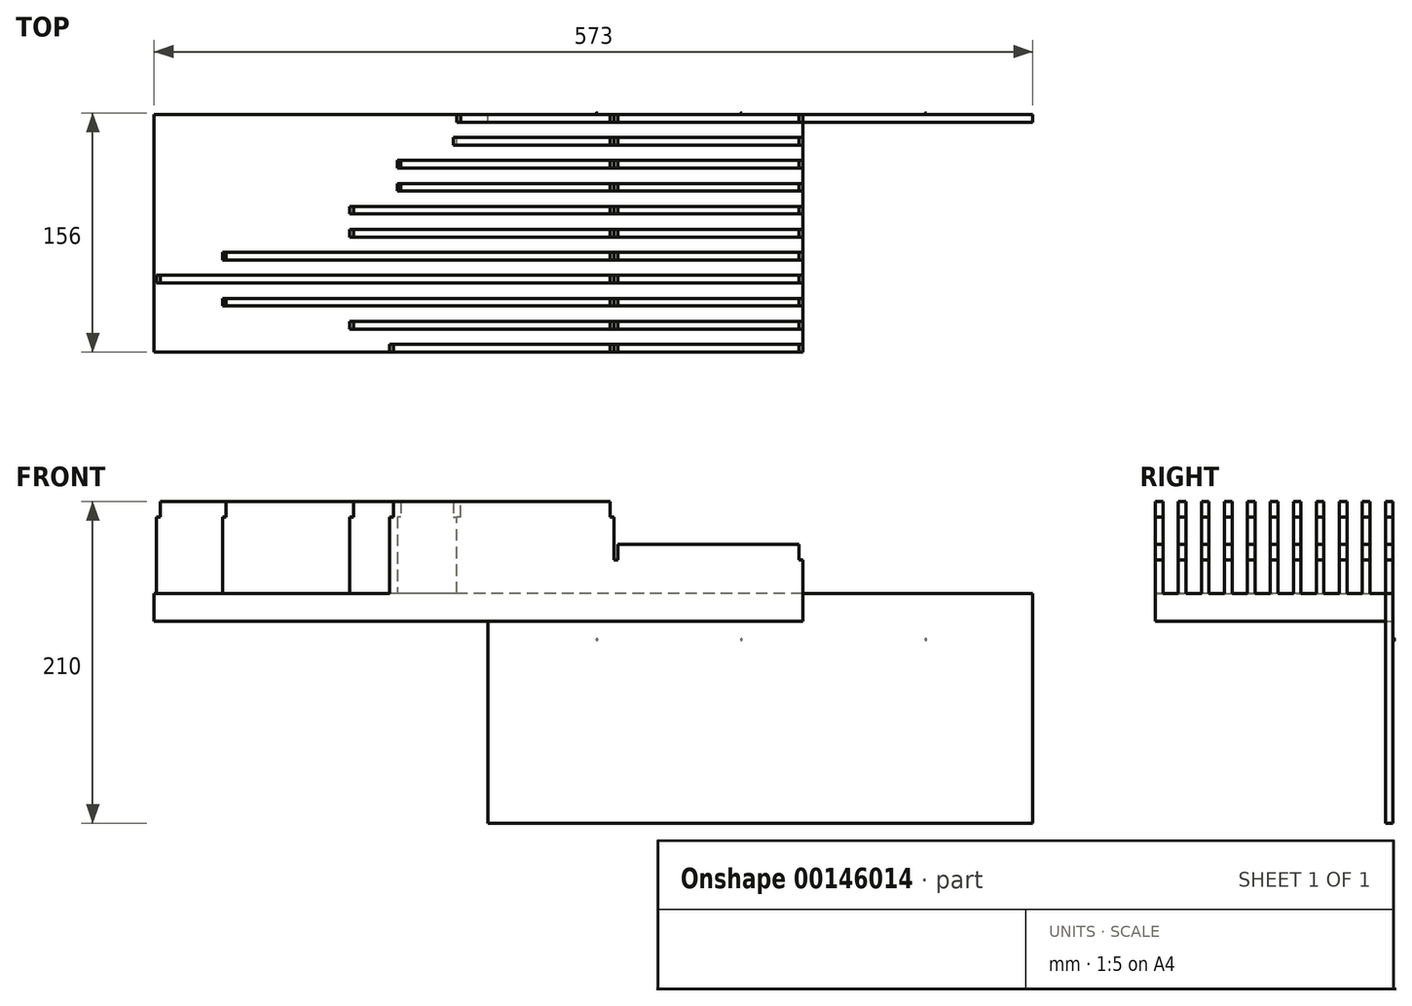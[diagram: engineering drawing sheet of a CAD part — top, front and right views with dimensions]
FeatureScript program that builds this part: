
annotation { "Feature Type Name" : "Feature", "Feature Type Description" : "" }
export const myFeature = defineFeature(function(context is Context, id is Id, definition is map)
    precondition{}
    {
        {
            var Q0;
            Q0=qCreatedBy(makeId("Right.planeOp"),FACE);
            var sketch = newSketch(context, id + "F0", { "sketchPlane" : qUnion([Q0])});
            skLineSegment(sketch, "E0", {"start": v(174.28, 60) * mm, "end": v(179.28, 60) * mm});
            skLineSegment(sketch, "E1", {"start": v(179.28, 60) * mm, "end": v(179.28, 0) * mm});
            skLineSegment(sketch, "E2", {"start": v(179.28, 0) * mm, "end": v(189.28, 0) * mm});
            skLineSegment(sketch, "E3", {"start": v(189.28, 0) * mm, "end": v(189.28, 60) * mm});
            skLineSegment(sketch, "E4", {"start": v(189.28, 60) * mm, "end": v(194.28, 60) * mm});
            skLineSegment(sketch, "E5", {"start": v(194.28, 60) * mm, "end": v(194.28, 0) * mm});
            skLineSegment(sketch, "E6", {"start": v(194.28, 0) * mm, "end": v(204.28, 0) * mm});
            skLineSegment(sketch, "E7", {"start": v(204.28, 0) * mm, "end": v(204.28, 60) * mm});
            skLineSegment(sketch, "E8", {"start": v(204.28, 60) * mm, "end": v(209.28, 60) * mm});
            skLineSegment(sketch, "E9", {"start": v(209.28, 60) * mm, "end": v(209.28, 0) * mm});
            skLineSegment(sketch, "E10", {"start": v(209.28, 0) * mm, "end": v(219.28, 0) * mm});
            skLineSegment(sketch, "E11", {"start": v(219.28, 0) * mm, "end": v(219.28, 60) * mm});
            skLineSegment(sketch, "E12", {"start": v(219.28, 60) * mm, "end": v(224.28, 60) * mm});
            skLineSegment(sketch, "E13", {"start": v(224.28, 60) * mm, "end": v(224.28, 0) * mm});
            skLineSegment(sketch, "E14", {"start": v(224.28, 0) * mm, "end": v(234.28, 0) * mm});
            skLineSegment(sketch, "E15", {"start": v(234.28, 0) * mm, "end": v(234.28, 60) * mm});
            skLineSegment(sketch, "E16", {"start": v(234.28, 60) * mm, "end": v(239.28, 60) * mm});
            skLineSegment(sketch, "E17", {"start": v(239.28, 60) * mm, "end": v(239.28, 0) * mm});
            skLineSegment(sketch, "E18", {"start": v(239.28, 0) * mm, "end": v(249.28, 0) * mm});
            skLineSegment(sketch, "E19", {"start": v(249.28, 0) * mm, "end": v(249.28, 60) * mm});
            skLineSegment(sketch, "E20", {"start": v(249.28, 60) * mm, "end": v(254.28, 60) * mm});
            skLineSegment(sketch, "E21", {"start": v(254.28, 60) * mm, "end": v(254.28, 0) * mm});
            skLineSegment(sketch, "E22", {"start": v(254.28, 0) * mm, "end": v(264.28, 0) * mm});
            skLineSegment(sketch, "E23", {"start": v(264.28, 0) * mm, "end": v(264.28, 60) * mm});
            skLineSegment(sketch, "E24", {"start": v(264.28, 60) * mm, "end": v(269.28, 60) * mm});
            skLineSegment(sketch, "E25", {"start": v(269.28, 60) * mm, "end": v(269.28, 0) * mm});
            skLineSegment(sketch, "E26", {"start": v(269.28, 0) * mm, "end": v(279.28, 0) * mm});
            skLineSegment(sketch, "E27", {"start": v(279.28, 0) * mm, "end": v(279.28, 60) * mm});
            skLineSegment(sketch, "E28", {"start": v(279.28, 60) * mm, "end": v(284.28, 60) * mm});
            skLineSegment(sketch, "E29", {"start": v(284.28, 60) * mm, "end": v(284.28, 0) * mm});
            skLineSegment(sketch, "E30", {"start": v(284.28, 0) * mm, "end": v(294.28, 0) * mm});
            skLineSegment(sketch, "E31", {"start": v(294.28, 0) * mm, "end": v(294.28, 60) * mm});
            skLineSegment(sketch, "E32", {"start": v(294.28, 60) * mm, "end": v(299.28, 60) * mm});
            skLineSegment(sketch, "E33", {"start": v(299.28, 60) * mm, "end": v(299.28, 0) * mm});
            skLineSegment(sketch, "E34", {"start": v(299.28, 0) * mm, "end": v(309.28, 0) * mm});
            skLineSegment(sketch, "E35", {"start": v(309.28, 0) * mm, "end": v(309.28, 60) * mm});
            skLineSegment(sketch, "E36", {"start": v(309.28, 60) * mm, "end": v(314.28, 60) * mm});
            skLineSegment(sketch, "E37", {"start": v(314.28, 60) * mm, "end": v(314.28, 0) * mm});
            skLineSegment(sketch, "E38", {"start": v(314.28, 0) * mm, "end": v(324.28, 0) * mm});
            skLineSegment(sketch, "E39", {"start": v(324.28, 0) * mm, "end": v(324.28, 60) * mm});
            skLineSegment(sketch, "E40", {"start": v(324.28, 60) * mm, "end": v(329.28, 60) * mm});
            skLineSegment(sketch, "E41", {"start": v(329.28, 60) * mm, "end": v(329.28, 60) * mm});
            skLineSegment(sketch, "E42", {"start": v(324.28, -18.06) * mm, "end": v(174.24, -18.06) * mm});
            skLineSegment(sketch, "E43", {"start": v(329.28, 60) * mm, "end": v(329.28, -150) * mm});
            skLineSegment(sketch, "E44", {"start": v(329.28, -150) * mm, "end": v(324.28, -150) * mm});
            skLineSegment(sketch, "E45", {"start": v(324.28, -150) * mm, "end": v(324.28, -18.06) * mm});
            skLineSegment(sketch, "E46", {"start": v(174.28, 60) * mm, "end": v(174.28, -18.06) * mm});
            skSolve(sketch);
        }
        {
            var Q0;
            Q0=makeQuery(id+"F0.imprint","IMPRINT",FACE,{"disambiguationData":[TD([[makeQuery(id+"F0.imprint","IMPRINT",EDGE,{"derivedFrom":sQuery(id+"F0.wireOp",EDGE,"RiP20wC8-9t7q-gec1-XB14-b4tMjAQ6knOq")}),-1.0]])]});
            var Q1;
            Q1=makeQuery(id+"F0.imprint","IMPRINT",FACE,{"disambiguationData":[TD([[makeQuery(id+"F0.imprint","IMPRINT",EDGE,{"derivedFrom":sQuery(id+"F0.wireOp",EDGE,"E0")}),-1.0]])]});
            extrude(context, id + "F1", {"entities" : qUnion([Q0, Q1]), "depth" : 123 * mm});
        }
        {
            var Q0;
            Q0 = qSketchRegion(id + "F0", true);
            extrude(context, id + "F2", {"entities" : qUnion([Q0]), "operationType" : NewBodyOperationType.ADD, "oppositeDirection" : true, "depth" : 300 * mm});
        }
        {
            var Q0;
            Q0=makeQuery(id+"F1.opExtrude","SWEPT_FACE",FACE,{"disambiguationData":[OSD([sQuery(id+"F0.wireOp",EDGE,"E43")])]});
            var sketch = newSketch(context, id + "F3", { "sketchPlane" : qUnion([Q0])});
            skCircle(sketch, "E47", {"center": v(-203.34, -30) * mm, "radius": 0.5 * mm});
            skCircle(sketch, "E48", {"center": v(-83.06, -30) * mm, "radius": 0.5 * mm});
            skCircle(sketch, "E49", {"center": v(11.19, -30) * mm, "radius": 0.5 * mm});
            skSolve(sketch);
        }
        {
            var Q0;
            Q0 = qSketchRegion(id + "F3", true);
            extrude(context, id + "F4", {"entities" : qUnion([Q0]), "operationType" : NewBodyOperationType.ADD, "depth" : 1 * mm});
        }
        {
            var Q0;
            Q0=makeQuery(id+"F1.opExtrude","SWEPT_FACE",FACE,{"disambiguationData":[OSD([sQuery(id+"F0.wireOp",EDGE,"E43")])]});
            var sketch = newSketch(context, id + "F5", { "sketchPlane" : qUnion([Q0])});
            skLineSegment(sketch, "E50.bottom", {"start": v(-123, 60) * mm, "end": v(0, 60) * mm});
            skLineSegment(sketch, "E50.top", {"start": v(-123, 32) * mm, "end": v(0, 32) * mm});
            skLineSegment(sketch, "E50.left", {"start": v(-123, 60) * mm, "end": v(-123, 32) * mm});
            skLineSegment(sketch, "E50.right", {"start": v(0, 60) * mm, "end": v(0, 32) * mm});
            skSolve(sketch);
        }
        {
            var Q0;
            Q0 = qSketchRegion(id + "F5", true);
            extrude(context, id + "F6", {"entities" : qUnion([Q0]), "operationType" : NewBodyOperationType.REMOVE, "oppositeDirection" : true, "depth" : 300 * mm});
        }
        {
            var Q0;
            Q0=makeQuery(id+"F1.opExtrude","SWEPT_FACE",FACE,{"disambiguationData":[OSD([sQuery(id+"F0.wireOp",EDGE,"E43")])]});
            var sketch = newSketch(context, id + "F7", { "sketchPlane" : qUnion([Q0])});
            skLineSegment(sketch, "E51.bottom", {"start": v(0, 32) * mm, "end": v(-2.5, 32) * mm});
            skLineSegment(sketch, "E51.top", {"start": v(0, 22) * mm, "end": v(-2.5, 22) * mm});
            skLineSegment(sketch, "E51.left", {"start": v(0, 32) * mm, "end": v(0, 22) * mm});
            skLineSegment(sketch, "E51.right", {"start": v(-2.5, 32) * mm, "end": v(-2.5, 22) * mm});
            skLineSegment(sketch, "E52.bottom", {"start": v(0, 60) * mm, "end": v(2.5, 60) * mm});
            skLineSegment(sketch, "E52.top", {"start": v(0, 50) * mm, "end": v(2.5, 50) * mm});
            skLineSegment(sketch, "E52.left", {"start": v(0, 60) * mm, "end": v(0, 50) * mm});
            skLineSegment(sketch, "E52.right", {"start": v(2.5, 60) * mm, "end": v(2.5, 50) * mm});
            skLineSegment(sketch, "E53.bottom", {"start": v(-123, 32) * mm, "end": v(-120.5, 32) * mm});
            skLineSegment(sketch, "E53.top", {"start": v(-123, 22) * mm, "end": v(-120.5, 22) * mm});
            skLineSegment(sketch, "E53.left", {"start": v(-123, 32) * mm, "end": v(-123, 22) * mm});
            skLineSegment(sketch, "E53.right", {"start": v(-120.5, 32) * mm, "end": v(-120.5, 22) * mm});
            skSolve(sketch);
        }
        {
            var Q0;
            Q0=makeQuery(id+"F7.imprint","IMPRINT",FACE,{"disambiguationData":[TD([[makeQuery(id+"F7.imprint","IMPRINT",EDGE,{"derivedFrom":sQuery(id+"F7.wireOp",EDGE,"E51.bottom")}),-1.0]])]});
            var Q1;
            Q1=makeQuery(id+"F7.imprint","IMPRINT",FACE,{"disambiguationData":[TD([[makeQuery(id+"F7.imprint","IMPRINT",EDGE,{"derivedFrom":sQuery(id+"F7.wireOp",EDGE,"E52.bottom")}),-1.0]])]});
            var Q2;
            Q2=makeQuery(id+"F7.imprint","IMPRINT",FACE,{"disambiguationData":[TD([[makeQuery(id+"F7.imprint","IMPRINT",EDGE,{"derivedFrom":sQuery(id+"F7.wireOp",EDGE,"E53.bottom")}),-1.0]])]});
            extrude(context, id + "F8", {"entities" : qUnion([Q0, Q1, Q2]), "operationType" : NewBodyOperationType.REMOVE, "oppositeDirection" : true, "depth" : 300 * mm});
        }
        {
            var Q0;
            Q0=makeQuery(id+"F1.opExtrude","SWEPT_FACE",FACE,{"disambiguationData":[OSD([sQuery(id+"F0.wireOp",EDGE,"E43")])]});
            var sketch = newSketch(context, id + "F9", { "sketchPlane" : qUnion([Q0])});
            skLineSegment(sketch, "E54.bottom", {"start": v(-123, -150) * mm, "end": v(-273, -150) * mm});
            skLineSegment(sketch, "E54.top", {"start": v(-123, 0) * mm, "end": v(-273, 0) * mm});
            skLineSegment(sketch, "E54.left", {"start": v(-123, -150) * mm, "end": v(-123, 0) * mm});
            skLineSegment(sketch, "E54.right", {"start": v(-273, -150) * mm, "end": v(-273, 0) * mm});
            skSolve(sketch);
        }
        {
            var Q0;
            Q0 = qSketchRegion(id + "F9", true);
            extrude(context, id + "F10", {"entities" : qUnion([Q0]), "operationType" : NewBodyOperationType.ADD, "oppositeDirection" : true, "depth" : 5 * mm});
        }
        {
            var Q0;
            Q0=makeQuery(id+"F2.opExtrude","CAP_FACE",FACE,{"disambiguationData":[OSD([sQuery(id+"F0.wireOp",EDGE,"E0"),sQuery(id+"F0.wireOp",EDGE,"E1"),sQuery(id+"F0.wireOp",EDGE,"E2"),sQuery(id+"F0.wireOp",EDGE,"E3"),sQuery(id+"F0.wireOp",EDGE,"E4"),sQuery(id+"F0.wireOp",EDGE,"E5"),sQuery(id+"F0.wireOp",EDGE,"E6"),sQuery(id+"F0.wireOp",EDGE,"E7"),sQuery(id+"F0.wireOp",EDGE,"E8"),sQuery(id+"F0.wireOp",EDGE,"E9"),sQuery(id+"F0.wireOp",EDGE,"E10"),sQuery(id+"F0.wireOp",EDGE,"E11"),sQuery(id+"F0.wireOp",EDGE,"E12"),sQuery(id+"F0.wireOp",EDGE,"E13"),sQuery(id+"F0.wireOp",EDGE,"E14"),sQuery(id+"F0.wireOp",EDGE,"E15"),sQuery(id+"F0.wireOp",EDGE,"E16"),sQuery(id+"F0.wireOp",EDGE,"E17"),sQuery(id+"F0.wireOp",EDGE,"E18"),sQuery(id+"F0.wireOp",EDGE,"E19"),sQuery(id+"F0.wireOp",EDGE,"E20"),sQuery(id+"F0.wireOp",EDGE,"E21"),sQuery(id+"F0.wireOp",EDGE,"E22"),sQuery(id+"F0.wireOp",EDGE,"E23"),sQuery(id+"F0.wireOp",EDGE,"E24"),sQuery(id+"F0.wireOp",EDGE,"E25"),sQuery(id+"F0.wireOp",EDGE,"E26"),sQuery(id+"F0.wireOp",EDGE,"E27"),sQuery(id+"F0.wireOp",EDGE,"E28"),sQuery(id+"F0.wireOp",EDGE,"E29"),sQuery(id+"F0.wireOp",EDGE,"E30"),sQuery(id+"F0.wireOp",EDGE,"E31"),sQuery(id+"F0.wireOp",EDGE,"E32"),sQuery(id+"F0.wireOp",EDGE,"E33"),sQuery(id+"F0.wireOp",EDGE,"E34"),sQuery(id+"F0.wireOp",EDGE,"E35"),sQuery(id+"F0.wireOp",EDGE,"E36"),sQuery(id+"F0.wireOp",EDGE,"E37"),sQuery(id+"F0.wireOp",EDGE,"E38"),sQuery(id+"F0.wireOp",EDGE,"E39"),sQuery(id+"F0.wireOp",EDGE,"E40"),sQuery(id+"F0.wireOp",EDGE,"E42"),sQuery(id+"F0.wireOp",EDGE,"E43"),sQuery(id+"F0.wireOp",EDGE,"E44"),sQuery(id+"F0.wireOp",EDGE,"E45"),sQuery(id+"F0.wireOp",EDGE,"E46")])],"isStart":false});
            var sketch = newSketch(context, id + "F11", { "sketchPlane" : qUnion([Q0])});
            skLineSegment(sketch, "E55.bottom", {"start": v(-309.28, 0) * mm, "end": v(-329.28, 0) * mm});
            skLineSegment(sketch, "E55.top", {"start": v(-309.28, 60) * mm, "end": v(-329.28, 60) * mm});
            skLineSegment(sketch, "E55.left", {"start": v(-309.28, 0) * mm, "end": v(-309.28, 60) * mm});
            skLineSegment(sketch, "E55.right", {"start": v(-329.28, 0) * mm, "end": v(-329.28, 60) * mm});
            skSolve(sketch);
        }
        {
            var Q0;
            {var subQ2=sQuery(id+"F11.wireOp",EDGE,"E55.right");Q0=makeQuery(id+"F11.imprint","IMPRINT",FACE,{"disambiguationData":[TD([[makeQuery(id+"F11.imprint","IMPRINT",EDGE,{"derivedFrom":subQ2}),1.0]])]});}
            var Q1;
            {var subQ0=sQuery(id+"F11.wireOp",EDGE,"E55.left");Q1=makeQuery(id+"F11.imprint","IMPRINT",FACE,{"disambiguationData":[TD([[makeQuery(id+"F11.imprint","IMPRINT",EDGE,{"derivedFrom":subQ0}),1.0]])]});}
            extrude(context, id + "F12", {"entities" : qUnion([Q0, Q1]), "operationType" : NewBodyOperationType.REMOVE, "oppositeDirection" : true, "depth" : 197.5 * mm});
        }
        {
            var Q0;
            Q0=makeQuery(id+"F2.opExtrude","CAP_FACE",FACE,{"disambiguationData":[OSD([sQuery(id+"F0.wireOp",EDGE,"E0"),sQuery(id+"F0.wireOp",EDGE,"E1"),sQuery(id+"F0.wireOp",EDGE,"E2"),sQuery(id+"F0.wireOp",EDGE,"E3"),sQuery(id+"F0.wireOp",EDGE,"E4"),sQuery(id+"F0.wireOp",EDGE,"E5"),sQuery(id+"F0.wireOp",EDGE,"E6"),sQuery(id+"F0.wireOp",EDGE,"E7"),sQuery(id+"F0.wireOp",EDGE,"E8"),sQuery(id+"F0.wireOp",EDGE,"E9"),sQuery(id+"F0.wireOp",EDGE,"E10"),sQuery(id+"F0.wireOp",EDGE,"E11"),sQuery(id+"F0.wireOp",EDGE,"E12"),sQuery(id+"F0.wireOp",EDGE,"E13"),sQuery(id+"F0.wireOp",EDGE,"E14"),sQuery(id+"F0.wireOp",EDGE,"E15"),sQuery(id+"F0.wireOp",EDGE,"E16"),sQuery(id+"F0.wireOp",EDGE,"E17"),sQuery(id+"F0.wireOp",EDGE,"E18"),sQuery(id+"F0.wireOp",EDGE,"E19"),sQuery(id+"F0.wireOp",EDGE,"E20"),sQuery(id+"F0.wireOp",EDGE,"E21"),sQuery(id+"F0.wireOp",EDGE,"E22"),sQuery(id+"F0.wireOp",EDGE,"E23"),sQuery(id+"F0.wireOp",EDGE,"E24"),sQuery(id+"F0.wireOp",EDGE,"E25"),sQuery(id+"F0.wireOp",EDGE,"E26"),sQuery(id+"F0.wireOp",EDGE,"E27"),sQuery(id+"F0.wireOp",EDGE,"E28"),sQuery(id+"F0.wireOp",EDGE,"E29"),sQuery(id+"F0.wireOp",EDGE,"E30"),sQuery(id+"F0.wireOp",EDGE,"E31"),sQuery(id+"F0.wireOp",EDGE,"E32"),sQuery(id+"F0.wireOp",EDGE,"E33"),sQuery(id+"F0.wireOp",EDGE,"E34"),sQuery(id+"F0.wireOp",EDGE,"E35"),sQuery(id+"F0.wireOp",EDGE,"E36"),sQuery(id+"F0.wireOp",EDGE,"E37"),sQuery(id+"F0.wireOp",EDGE,"E38"),sQuery(id+"F0.wireOp",EDGE,"E39"),sQuery(id+"F0.wireOp",EDGE,"E40"),sQuery(id+"F0.wireOp",EDGE,"E42"),sQuery(id+"F0.wireOp",EDGE,"E43"),sQuery(id+"F0.wireOp",EDGE,"E44"),sQuery(id+"F0.wireOp",EDGE,"E45"),sQuery(id+"F0.wireOp",EDGE,"E46")])],"isStart":false});
            var sketch = newSketch(context, id + "F13", { "sketchPlane" : qUnion([Q0])});
            skLineSegment(sketch, "E56.bottom", {"start": v(-279.28, 0) * mm, "end": v(-299.28, 0) * mm});
            skLineSegment(sketch, "E56.top", {"start": v(-279.28, 60) * mm, "end": v(-299.28, 60) * mm});
            skLineSegment(sketch, "E56.left", {"start": v(-279.28, 0) * mm, "end": v(-279.28, 60) * mm});
            skLineSegment(sketch, "E56.right", {"start": v(-299.28, 0) * mm, "end": v(-299.28, 60) * mm});
            skSolve(sketch);
        }
        {
            var Q0;
            Q0 = qSketchRegion(id + "F13", true);
            extrude(context, id + "F14", {"entities" : qUnion([Q0]), "operationType" : NewBodyOperationType.REMOVE, "oppositeDirection" : true, "depth" : 158.5 * mm});
        }
        {
            var Q0;
            Q0=makeQuery(id+"F2.opExtrude","CAP_FACE",FACE,{"disambiguationData":[OSD([sQuery(id+"F0.wireOp",EDGE,"E0"),sQuery(id+"F0.wireOp",EDGE,"E1"),sQuery(id+"F0.wireOp",EDGE,"E2"),sQuery(id+"F0.wireOp",EDGE,"E3"),sQuery(id+"F0.wireOp",EDGE,"E4"),sQuery(id+"F0.wireOp",EDGE,"E5"),sQuery(id+"F0.wireOp",EDGE,"E6"),sQuery(id+"F0.wireOp",EDGE,"E7"),sQuery(id+"F0.wireOp",EDGE,"E8"),sQuery(id+"F0.wireOp",EDGE,"E9"),sQuery(id+"F0.wireOp",EDGE,"E10"),sQuery(id+"F0.wireOp",EDGE,"E11"),sQuery(id+"F0.wireOp",EDGE,"E12"),sQuery(id+"F0.wireOp",EDGE,"E13"),sQuery(id+"F0.wireOp",EDGE,"E14"),sQuery(id+"F0.wireOp",EDGE,"E15"),sQuery(id+"F0.wireOp",EDGE,"E16"),sQuery(id+"F0.wireOp",EDGE,"E17"),sQuery(id+"F0.wireOp",EDGE,"E18"),sQuery(id+"F0.wireOp",EDGE,"E19"),sQuery(id+"F0.wireOp",EDGE,"E20"),sQuery(id+"F0.wireOp",EDGE,"E21"),sQuery(id+"F0.wireOp",EDGE,"E22"),sQuery(id+"F0.wireOp",EDGE,"E23"),sQuery(id+"F0.wireOp",EDGE,"E24"),sQuery(id+"F0.wireOp",EDGE,"E25"),sQuery(id+"F0.wireOp",EDGE,"E26"),sQuery(id+"F0.wireOp",EDGE,"E27"),sQuery(id+"F0.wireOp",EDGE,"E28"),sQuery(id+"F0.wireOp",EDGE,"E29"),sQuery(id+"F0.wireOp",EDGE,"E30"),sQuery(id+"F0.wireOp",EDGE,"E31"),sQuery(id+"F0.wireOp",EDGE,"E32"),sQuery(id+"F0.wireOp",EDGE,"E33"),sQuery(id+"F0.wireOp",EDGE,"E34"),sQuery(id+"F0.wireOp",EDGE,"E35"),sQuery(id+"F0.wireOp",EDGE,"E36"),sQuery(id+"F0.wireOp",EDGE,"E37"),sQuery(id+"F0.wireOp",EDGE,"E38"),sQuery(id+"F0.wireOp",EDGE,"E39"),sQuery(id+"F0.wireOp",EDGE,"E40"),sQuery(id+"F0.wireOp",EDGE,"E42"),sQuery(id+"F0.wireOp",EDGE,"E43"),sQuery(id+"F0.wireOp",EDGE,"E44"),sQuery(id+"F0.wireOp",EDGE,"E45"),sQuery(id+"F0.wireOp",EDGE,"E46")])],"isStart":false});
            var sketch = newSketch(context, id + "F15", { "sketchPlane" : qUnion([Q0])});
            skLineSegment(sketch, "E57.bottom", {"start": v(-269.28, 60) * mm, "end": v(-249.28, 60) * mm});
            skLineSegment(sketch, "E57.top", {"start": v(-269.28, 0) * mm, "end": v(-249.28, 0) * mm});
            skLineSegment(sketch, "E57.left", {"start": v(-269.28, 60) * mm, "end": v(-269.28, 0) * mm});
            skLineSegment(sketch, "E57.right", {"start": v(-249.28, 60) * mm, "end": v(-249.28, 0) * mm});
            skLineSegment(sketch, "E58.bottom", {"start": v(-194.28, 0) * mm, "end": v(-189.28, 0) * mm});
            skLineSegment(sketch, "E58.top", {"start": v(-194.28, 60) * mm, "end": v(-189.28, 60) * mm});
            skLineSegment(sketch, "E58.left", {"start": v(-194.28, 0) * mm, "end": v(-194.28, 60) * mm});
            skLineSegment(sketch, "E58.right", {"start": v(-189.28, 0) * mm, "end": v(-189.28, 60) * mm});
            skSolve(sketch);
        }
        {
            var Q0;
            Q0 = qSketchRegion(id + "F15", true);
            extrude(context, id + "F16", {"entities" : qUnion([Q0]), "operationType" : NewBodyOperationType.REMOVE, "oppositeDirection" : true, "depth" : 127.5 * mm});
        }
        {
            var Q0;
            Q0=makeQuery(id+"F2.opExtrude","CAP_FACE",FACE,{"disambiguationData":[OSD([sQuery(id+"F0.wireOp",EDGE,"E0"),sQuery(id+"F0.wireOp",EDGE,"E1"),sQuery(id+"F0.wireOp",EDGE,"E2"),sQuery(id+"F0.wireOp",EDGE,"E3"),sQuery(id+"F0.wireOp",EDGE,"E4"),sQuery(id+"F0.wireOp",EDGE,"E5"),sQuery(id+"F0.wireOp",EDGE,"E6"),sQuery(id+"F0.wireOp",EDGE,"E7"),sQuery(id+"F0.wireOp",EDGE,"E8"),sQuery(id+"F0.wireOp",EDGE,"E9"),sQuery(id+"F0.wireOp",EDGE,"E10"),sQuery(id+"F0.wireOp",EDGE,"E11"),sQuery(id+"F0.wireOp",EDGE,"E12"),sQuery(id+"F0.wireOp",EDGE,"E13"),sQuery(id+"F0.wireOp",EDGE,"E14"),sQuery(id+"F0.wireOp",EDGE,"E15"),sQuery(id+"F0.wireOp",EDGE,"E16"),sQuery(id+"F0.wireOp",EDGE,"E17"),sQuery(id+"F0.wireOp",EDGE,"E18"),sQuery(id+"F0.wireOp",EDGE,"E19"),sQuery(id+"F0.wireOp",EDGE,"E20"),sQuery(id+"F0.wireOp",EDGE,"E21"),sQuery(id+"F0.wireOp",EDGE,"E22"),sQuery(id+"F0.wireOp",EDGE,"E23"),sQuery(id+"F0.wireOp",EDGE,"E24"),sQuery(id+"F0.wireOp",EDGE,"E25"),sQuery(id+"F0.wireOp",EDGE,"E26"),sQuery(id+"F0.wireOp",EDGE,"E27"),sQuery(id+"F0.wireOp",EDGE,"E28"),sQuery(id+"F0.wireOp",EDGE,"E29"),sQuery(id+"F0.wireOp",EDGE,"E30"),sQuery(id+"F0.wireOp",EDGE,"E31"),sQuery(id+"F0.wireOp",EDGE,"E32"),sQuery(id+"F0.wireOp",EDGE,"E33"),sQuery(id+"F0.wireOp",EDGE,"E34"),sQuery(id+"F0.wireOp",EDGE,"E35"),sQuery(id+"F0.wireOp",EDGE,"E36"),sQuery(id+"F0.wireOp",EDGE,"E37"),sQuery(id+"F0.wireOp",EDGE,"E38"),sQuery(id+"F0.wireOp",EDGE,"E39"),sQuery(id+"F0.wireOp",EDGE,"E40"),sQuery(id+"F0.wireOp",EDGE,"E42"),sQuery(id+"F0.wireOp",EDGE,"E43"),sQuery(id+"F0.wireOp",EDGE,"E44"),sQuery(id+"F0.wireOp",EDGE,"E45"),sQuery(id+"F0.wireOp",EDGE,"E46")])],"isStart":false});
            var sketch = newSketch(context, id + "F17", { "sketchPlane" : qUnion([Q0])});
            skLineSegment(sketch, "E59.bottom", {"start": v(-239.28, 60) * mm, "end": v(-234.28, 60) * mm});
            skLineSegment(sketch, "E59.top", {"start": v(-239.28, 0) * mm, "end": v(-234.28, 0) * mm});
            skLineSegment(sketch, "E59.left", {"start": v(-239.28, 60) * mm, "end": v(-239.28, 0) * mm});
            skLineSegment(sketch, "E59.right", {"start": v(-234.28, 60) * mm, "end": v(-234.28, 0) * mm});
            skLineSegment(sketch, "E60.bottom", {"start": v(-209.28, 60) * mm, "end": v(-204.28, 60) * mm});
            skLineSegment(sketch, "E60.top", {"start": v(-209.28, 0) * mm, "end": v(-204.28, 0) * mm});
            skLineSegment(sketch, "E60.left", {"start": v(-209.28, 60) * mm, "end": v(-209.28, 0) * mm});
            skLineSegment(sketch, "E60.right", {"start": v(-204.28, 60) * mm, "end": v(-204.28, 0) * mm});
            skSolve(sketch);
        }
        {
            var Q0;
            Q0 = qSketchRegion(id + "F17", true);
            extrude(context, id + "F18", {"entities" : qUnion([Q0]), "operationType" : NewBodyOperationType.REMOVE, "oppositeDirection" : true, "depth" : 44.5 * mm});
        }
        {
            var Q0;
            Q0=makeQuery(id+"F2.opExtrude","CAP_FACE",FACE,{"disambiguationData":[OSD([sQuery(id+"F0.wireOp",EDGE,"E0"),sQuery(id+"F0.wireOp",EDGE,"E1"),sQuery(id+"F0.wireOp",EDGE,"E2"),sQuery(id+"F0.wireOp",EDGE,"E3"),sQuery(id+"F0.wireOp",EDGE,"E4"),sQuery(id+"F0.wireOp",EDGE,"E5"),sQuery(id+"F0.wireOp",EDGE,"E6"),sQuery(id+"F0.wireOp",EDGE,"E7"),sQuery(id+"F0.wireOp",EDGE,"E8"),sQuery(id+"F0.wireOp",EDGE,"E9"),sQuery(id+"F0.wireOp",EDGE,"E10"),sQuery(id+"F0.wireOp",EDGE,"E11"),sQuery(id+"F0.wireOp",EDGE,"E12"),sQuery(id+"F0.wireOp",EDGE,"E13"),sQuery(id+"F0.wireOp",EDGE,"E14"),sQuery(id+"F0.wireOp",EDGE,"E15"),sQuery(id+"F0.wireOp",EDGE,"E16"),sQuery(id+"F0.wireOp",EDGE,"E17"),sQuery(id+"F0.wireOp",EDGE,"E18"),sQuery(id+"F0.wireOp",EDGE,"E19"),sQuery(id+"F0.wireOp",EDGE,"E20"),sQuery(id+"F0.wireOp",EDGE,"E21"),sQuery(id+"F0.wireOp",EDGE,"E22"),sQuery(id+"F0.wireOp",EDGE,"E23"),sQuery(id+"F0.wireOp",EDGE,"E24"),sQuery(id+"F0.wireOp",EDGE,"E25"),sQuery(id+"F0.wireOp",EDGE,"E26"),sQuery(id+"F0.wireOp",EDGE,"E27"),sQuery(id+"F0.wireOp",EDGE,"E28"),sQuery(id+"F0.wireOp",EDGE,"E29"),sQuery(id+"F0.wireOp",EDGE,"E30"),sQuery(id+"F0.wireOp",EDGE,"E31"),sQuery(id+"F0.wireOp",EDGE,"E32"),sQuery(id+"F0.wireOp",EDGE,"E33"),sQuery(id+"F0.wireOp",EDGE,"E34"),sQuery(id+"F0.wireOp",EDGE,"E35"),sQuery(id+"F0.wireOp",EDGE,"E36"),sQuery(id+"F0.wireOp",EDGE,"E37"),sQuery(id+"F0.wireOp",EDGE,"E38"),sQuery(id+"F0.wireOp",EDGE,"E39"),sQuery(id+"F0.wireOp",EDGE,"E40"),sQuery(id+"F0.wireOp",EDGE,"E42"),sQuery(id+"F0.wireOp",EDGE,"E43"),sQuery(id+"F0.wireOp",EDGE,"E44"),sQuery(id+"F0.wireOp",EDGE,"E45"),sQuery(id+"F0.wireOp",EDGE,"E46")])],"isStart":false});
            var sketch = newSketch(context, id + "F19", { "sketchPlane" : qUnion([Q0])});
            skLineSegment(sketch, "E61.bottom", {"start": v(-219.28, 0) * mm, "end": v(-224.28, 0) * mm});
            skLineSegment(sketch, "E61.top", {"start": v(-219.28, 60) * mm, "end": v(-224.28, 60) * mm});
            skLineSegment(sketch, "E61.left", {"start": v(-219.28, 0) * mm, "end": v(-219.28, 60) * mm});
            skLineSegment(sketch, "E61.right", {"start": v(-224.28, 0) * mm, "end": v(-224.28, 60) * mm});
            skSolve(sketch);
        }
        {
            var Q0;
            Q0 = qSketchRegion(id + "F19", true);
            extrude(context, id + "F20", {"entities" : qUnion([Q0]), "operationType" : NewBodyOperationType.REMOVE, "oppositeDirection" : true, "depth" : 1.5 * mm});
        }
        {
            var Q0;
            Q0=makeQuery(id+"F2.opExtrude","CAP_FACE",FACE,{"disambiguationData":[OSD([sQuery(id+"F0.wireOp",EDGE,"E0"),sQuery(id+"F0.wireOp",EDGE,"E1"),sQuery(id+"F0.wireOp",EDGE,"E2"),sQuery(id+"F0.wireOp",EDGE,"E3"),sQuery(id+"F0.wireOp",EDGE,"E4"),sQuery(id+"F0.wireOp",EDGE,"E5"),sQuery(id+"F0.wireOp",EDGE,"E6"),sQuery(id+"F0.wireOp",EDGE,"E7"),sQuery(id+"F0.wireOp",EDGE,"E8"),sQuery(id+"F0.wireOp",EDGE,"E9"),sQuery(id+"F0.wireOp",EDGE,"E10"),sQuery(id+"F0.wireOp",EDGE,"E11"),sQuery(id+"F0.wireOp",EDGE,"E12"),sQuery(id+"F0.wireOp",EDGE,"E13"),sQuery(id+"F0.wireOp",EDGE,"E14"),sQuery(id+"F0.wireOp",EDGE,"E15"),sQuery(id+"F0.wireOp",EDGE,"E16"),sQuery(id+"F0.wireOp",EDGE,"E17"),sQuery(id+"F0.wireOp",EDGE,"E18"),sQuery(id+"F0.wireOp",EDGE,"E19"),sQuery(id+"F0.wireOp",EDGE,"E20"),sQuery(id+"F0.wireOp",EDGE,"E21"),sQuery(id+"F0.wireOp",EDGE,"E22"),sQuery(id+"F0.wireOp",EDGE,"E23"),sQuery(id+"F0.wireOp",EDGE,"E24"),sQuery(id+"F0.wireOp",EDGE,"E25"),sQuery(id+"F0.wireOp",EDGE,"E26"),sQuery(id+"F0.wireOp",EDGE,"E27"),sQuery(id+"F0.wireOp",EDGE,"E28"),sQuery(id+"F0.wireOp",EDGE,"E29"),sQuery(id+"F0.wireOp",EDGE,"E30"),sQuery(id+"F0.wireOp",EDGE,"E31"),sQuery(id+"F0.wireOp",EDGE,"E32"),sQuery(id+"F0.wireOp",EDGE,"E33"),sQuery(id+"F0.wireOp",EDGE,"E34"),sQuery(id+"F0.wireOp",EDGE,"E35"),sQuery(id+"F0.wireOp",EDGE,"E36"),sQuery(id+"F0.wireOp",EDGE,"E37"),sQuery(id+"F0.wireOp",EDGE,"E38"),sQuery(id+"F0.wireOp",EDGE,"E39"),sQuery(id+"F0.wireOp",EDGE,"E40"),sQuery(id+"F0.wireOp",EDGE,"E42"),sQuery(id+"F0.wireOp",EDGE,"E43"),sQuery(id+"F0.wireOp",EDGE,"E44"),sQuery(id+"F0.wireOp",EDGE,"E45"),sQuery(id+"F0.wireOp",EDGE,"E46")])],"isStart":false});
            var sketch = newSketch(context, id + "F21", { "sketchPlane" : qUnion([Q0])});
            skLineSegment(sketch, "E62.bottom", {"start": v(-179.28, 0) * mm, "end": v(-174.28, 0) * mm});
            skLineSegment(sketch, "E62.top", {"start": v(-179.28, 60) * mm, "end": v(-174.28, 60) * mm});
            skLineSegment(sketch, "E62.left", {"start": v(-179.28, 0) * mm, "end": v(-179.28, 60) * mm});
            skLineSegment(sketch, "E62.right", {"start": v(-174.28, 0) * mm, "end": v(-174.28, 60) * mm});
            skSolve(sketch);
        }
        {
            var Q0;
            Q0 = qSketchRegion(id + "F21", true);
            extrude(context, id + "F22", {"entities" : qUnion([Q0]), "operationType" : NewBodyOperationType.REMOVE, "oppositeDirection" : true, "depth" : 153.5 * mm});
        }
        {
            var Q0;
            Q0=makeQuery(id+"F20.boolean.opBoolean","COPY",FACE,{"derivedFrom":makeQuery(id+"F20.opExtrude","CAP_FACE",FACE,{"disambiguationData":[OSD([sQuery(id+"F19.wireOp",EDGE,"E61.bottom"),sQuery(id+"F19.wireOp",EDGE,"E61.top"),sQuery(id+"F19.wireOp",EDGE,"E61.left"),sQuery(id+"F19.wireOp",EDGE,"E61.right")])],"isStart":false})});
            var sketch = newSketch(context, id + "F23", { "sketchPlane" : qUnion([Q0])});
            skLineSegment(sketch, "E63.bottom", {"start": v(-224.28, 60) * mm, "end": v(-219.28, 60) * mm});
            skLineSegment(sketch, "E63.top", {"start": v(-224.28, 50) * mm, "end": v(-219.28, 50) * mm});
            skLineSegment(sketch, "E63.left", {"start": v(-224.28, 60) * mm, "end": v(-224.28, 50) * mm});
            skLineSegment(sketch, "E63.right", {"start": v(-219.28, 60) * mm, "end": v(-219.28, 50) * mm});
            skSolve(sketch);
        }
        {
            var Q0;
            Q0 = qSketchRegion(id + "F23", true);
            extrude(context, id + "F24", {"entities" : qUnion([Q0]), "operationType" : NewBodyOperationType.REMOVE, "oppositeDirection" : true, "depth" : 2.5 * mm});
        }
        {
            var Q0;
            Q0=makeQuery(id+"F18.boolean.opBoolean","COPY",FACE,{"derivedFrom":makeQuery(id+"F18.opExtrude","CAP_FACE",FACE,{"disambiguationData":[OSD([sQuery(id+"F17.wireOp",EDGE,"E59.bottom"),sQuery(id+"F17.wireOp",EDGE,"E59.top"),sQuery(id+"F17.wireOp",EDGE,"E59.left"),sQuery(id+"F17.wireOp",EDGE,"E59.right")])],"isStart":false})});
            var sketch = newSketch(context, id + "F25", { "sketchPlane" : qUnion([Q0])});
            skLineSegment(sketch, "E64.bottom", {"start": v(-239.28, 60) * mm, "end": v(-234.28, 60) * mm});
            skLineSegment(sketch, "E64.top", {"start": v(-239.28, 50) * mm, "end": v(-234.28, 50) * mm});
            skLineSegment(sketch, "E64.left", {"start": v(-239.28, 60) * mm, "end": v(-239.28, 50) * mm});
            skLineSegment(sketch, "E64.right", {"start": v(-234.28, 60) * mm, "end": v(-234.28, 50) * mm});
            skSolve(sketch);
        }
        {
            var Q0;
            Q0 = qSketchRegion(id + "F25", true);
            extrude(context, id + "F26", {"entities" : qUnion([Q0]), "operationType" : NewBodyOperationType.REMOVE, "oppositeDirection" : true, "depth" : 2.5 * mm});
        }
        {
            var Q0;
            Q0=makeQuery(id+"F18.boolean.opBoolean","COPY",FACE,{"derivedFrom":makeQuery(id+"F18.opExtrude","CAP_FACE",FACE,{"disambiguationData":[OSD([sQuery(id+"F17.wireOp",EDGE,"E60.bottom"),sQuery(id+"F17.wireOp",EDGE,"E60.top"),sQuery(id+"F17.wireOp",EDGE,"E60.left"),sQuery(id+"F17.wireOp",EDGE,"E60.right")])],"isStart":false})});
            var sketch = newSketch(context, id + "F27", { "sketchPlane" : qUnion([Q0])});
            skLineSegment(sketch, "E65.bottom", {"start": v(-209.28, 60) * mm, "end": v(-204.28, 60) * mm});
            skLineSegment(sketch, "E65.top", {"start": v(-209.28, 50) * mm, "end": v(-204.28, 50) * mm});
            skLineSegment(sketch, "E65.left", {"start": v(-209.28, 60) * mm, "end": v(-209.28, 50) * mm});
            skLineSegment(sketch, "E65.right", {"start": v(-204.28, 60) * mm, "end": v(-204.28, 50) * mm});
            skSolve(sketch);
        }
        {
            var Q0;
            Q0 = qSketchRegion(id + "F27", true);
            extrude(context, id + "F28", {"entities" : qUnion([Q0]), "operationType" : NewBodyOperationType.REMOVE, "oppositeDirection" : true, "depth" : 2.5 * mm});
        }
        {
            var Q0;
            {var subQ7=sQuery(id+"F0.wireOp",EDGE,"E19");var subQ10=sQuery(id+"F15.wireOp",EDGE,"E57.top");Q0=makeQuery(id+"F16.boolean.opBoolean","COPY",FACE,{"disambiguationData":[TD([makeQuery(id+"F1.opExtrude","SWEPT_FACE",FACE,{"disambiguationData":[OSD([subQ7])]})])],"derivedFrom":makeQuery(id+"F16.opExtrude","CAP_FACE",FACE,{"disambiguationData":[OSD([sQuery(id+"F15.wireOp",EDGE,"E57.bottom"),subQ10,sQuery(id+"F15.wireOp",EDGE,"E57.left"),sQuery(id+"F15.wireOp",EDGE,"E57.right")])],"isStart":false})});}
            var sketch = newSketch(context, id + "F29", { "sketchPlane" : qUnion([Q0])});
            skLineSegment(sketch, "E66.bottom", {"start": v(-254.28, 60) * mm, "end": v(-249.28, 60) * mm});
            skLineSegment(sketch, "E66.top", {"start": v(-254.28, 50) * mm, "end": v(-249.28, 50) * mm});
            skLineSegment(sketch, "E66.left", {"start": v(-254.28, 60) * mm, "end": v(-254.28, 50) * mm});
            skLineSegment(sketch, "E66.right", {"start": v(-249.28, 60) * mm, "end": v(-249.28, 50) * mm});
            skSolve(sketch);
        }
        {
            var Q0;
            Q0 = qSketchRegion(id + "F29", true);
            extrude(context, id + "F30", {"entities" : qUnion([Q0]), "operationType" : NewBodyOperationType.REMOVE, "oppositeDirection" : true, "depth" : 2.5 * mm});
        }
        {
            var Q0;
            Q0=makeQuery(id+"F16.boolean.opBoolean","COPY",FACE,{"derivedFrom":makeQuery(id+"F16.opExtrude","CAP_FACE",FACE,{"disambiguationData":[OSD([sQuery(id+"F15.wireOp",EDGE,"E58.bottom"),sQuery(id+"F15.wireOp",EDGE,"E58.top"),sQuery(id+"F15.wireOp",EDGE,"E58.left"),sQuery(id+"F15.wireOp",EDGE,"E58.right")])],"isStart":false})});
            var sketch = newSketch(context, id + "F31", { "sketchPlane" : qUnion([Q0])});
            skLineSegment(sketch, "E67.bottom", {"start": v(-194.28, 60) * mm, "end": v(-189.28, 60) * mm});
            skLineSegment(sketch, "E67.top", {"start": v(-194.28, 50) * mm, "end": v(-189.28, 50) * mm});
            skLineSegment(sketch, "E67.left", {"start": v(-194.28, 60) * mm, "end": v(-194.28, 50) * mm});
            skLineSegment(sketch, "E67.right", {"start": v(-189.28, 60) * mm, "end": v(-189.28, 50) * mm});
            skSolve(sketch);
        }
        {
            var Q0;
            Q0 = qSketchRegion(id + "F31", true);
            extrude(context, id + "F32", {"entities" : qUnion([Q0]), "operationType" : NewBodyOperationType.REMOVE, "oppositeDirection" : true, "depth" : 2.5 * mm});
        }
        {
            var Q0;
            {var subQ3=sQuery(id+"F0.wireOp",EDGE,"E23");var subQ10=sQuery(id+"F15.wireOp",EDGE,"E57.top");Q0=makeQuery(id+"F16.boolean.opBoolean","COPY",FACE,{"disambiguationData":[TD([makeQuery(id+"F1.opExtrude","SWEPT_FACE",FACE,{"disambiguationData":[OSD([subQ3])]})])],"derivedFrom":makeQuery(id+"F16.opExtrude","CAP_FACE",FACE,{"disambiguationData":[OSD([sQuery(id+"F15.wireOp",EDGE,"E57.bottom"),subQ10,sQuery(id+"F15.wireOp",EDGE,"E57.left"),sQuery(id+"F15.wireOp",EDGE,"E57.right")])],"isStart":false})});}
            var sketch = newSketch(context, id + "F33", { "sketchPlane" : qUnion([Q0])});
            skLineSegment(sketch, "E68.bottom", {"start": v(-269.28, 60) * mm, "end": v(-264.28, 60) * mm});
            skLineSegment(sketch, "E68.top", {"start": v(-269.28, 50) * mm, "end": v(-264.28, 50) * mm});
            skLineSegment(sketch, "E68.left", {"start": v(-269.28, 60) * mm, "end": v(-269.28, 50) * mm});
            skLineSegment(sketch, "E68.right", {"start": v(-264.28, 60) * mm, "end": v(-264.28, 50) * mm});
            skSolve(sketch);
        }
        {
            var Q0;
            Q0 = qSketchRegion(id + "F33", true);
            extrude(context, id + "F34", {"entities" : qUnion([Q0]), "operationType" : NewBodyOperationType.REMOVE, "oppositeDirection" : true, "depth" : 2.5 * mm});
        }
        {
            var Q0;
            Q0=makeQuery(id+"F22.boolean.opBoolean","COPY",FACE,{"derivedFrom":makeQuery(id+"F22.opExtrude","CAP_FACE",FACE,{"disambiguationData":[OSD([sQuery(id+"F21.wireOp",EDGE,"E62.bottom"),sQuery(id+"F21.wireOp",EDGE,"E62.top"),sQuery(id+"F21.wireOp",EDGE,"E62.left"),sQuery(id+"F21.wireOp",EDGE,"E62.right")])],"isStart":false})});
            var sketch = newSketch(context, id + "F35", { "sketchPlane" : qUnion([Q0])});
            skLineSegment(sketch, "E69.bottom", {"start": v(-179.28, 60) * mm, "end": v(-174.28, 60) * mm});
            skLineSegment(sketch, "E69.top", {"start": v(-179.28, 50) * mm, "end": v(-174.28, 50) * mm});
            skLineSegment(sketch, "E69.left", {"start": v(-179.28, 60) * mm, "end": v(-179.28, 50) * mm});
            skLineSegment(sketch, "E69.right", {"start": v(-174.28, 60) * mm, "end": v(-174.28, 50) * mm});
            skSolve(sketch);
        }
        {
            var Q0;
            Q0 = qSketchRegion(id + "F35", true);
            extrude(context, id + "F36", {"entities" : qUnion([Q0]), "operationType" : NewBodyOperationType.REMOVE, "oppositeDirection" : true, "depth" : 2.5 * mm});
        }
        {
            var Q0;
            {var subQ3=sQuery(id+"F0.wireOp",EDGE,"E27");var subQ7=sQuery(id+"F13.wireOp",EDGE,"E56.bottom");Q0=makeQuery(id+"F14.boolean.opBoolean","COPY",FACE,{"disambiguationData":[TD([makeQuery(id+"F1.opExtrude","SWEPT_FACE",FACE,{"disambiguationData":[OSD([subQ3])]})])],"derivedFrom":makeQuery(id+"F14.opExtrude","CAP_FACE",FACE,{"disambiguationData":[OSD([subQ7,sQuery(id+"F13.wireOp",EDGE,"E56.top"),sQuery(id+"F13.wireOp",EDGE,"E56.left"),sQuery(id+"F13.wireOp",EDGE,"E56.right")])],"isStart":false})});}
            var sketch = newSketch(context, id + "F37", { "sketchPlane" : qUnion([Q0])});
            skLineSegment(sketch, "E70.bottom", {"start": v(-284.28, 60) * mm, "end": v(-279.28, 60) * mm});
            skLineSegment(sketch, "E70.top", {"start": v(-284.28, 50) * mm, "end": v(-279.28, 50) * mm});
            skLineSegment(sketch, "E70.left", {"start": v(-284.28, 60) * mm, "end": v(-284.28, 50) * mm});
            skLineSegment(sketch, "E70.right", {"start": v(-279.28, 60) * mm, "end": v(-279.28, 50) * mm});
            skSolve(sketch);
        }
        {
            var Q0;
            Q0 = qSketchRegion(id + "F37", true);
            extrude(context, id + "F38", {"entities" : qUnion([Q0]), "operationType" : NewBodyOperationType.REMOVE, "oppositeDirection" : true, "depth" : 2.5 * mm});
        }
        {
            var Q0;
            {var subQ0=sQuery(id+"F0.wireOp",EDGE,"E31");var subQ7=sQuery(id+"F13.wireOp",EDGE,"E56.bottom");Q0=makeQuery(id+"F14.boolean.opBoolean","COPY",FACE,{"disambiguationData":[TD([makeQuery(id+"F1.opExtrude","SWEPT_FACE",FACE,{"disambiguationData":[OSD([subQ0])]})])],"derivedFrom":makeQuery(id+"F14.opExtrude","CAP_FACE",FACE,{"disambiguationData":[OSD([subQ7,sQuery(id+"F13.wireOp",EDGE,"E56.top"),sQuery(id+"F13.wireOp",EDGE,"E56.left"),sQuery(id+"F13.wireOp",EDGE,"E56.right")])],"isStart":false})});}
            var sketch = newSketch(context, id + "F39", { "sketchPlane" : qUnion([Q0])});
            skLineSegment(sketch, "E71.bottom", {"start": v(-299.28, 60) * mm, "end": v(-294.28, 60) * mm});
            skLineSegment(sketch, "E71.top", {"start": v(-299.28, 50) * mm, "end": v(-294.28, 50) * mm});
            skLineSegment(sketch, "E71.left", {"start": v(-299.28, 60) * mm, "end": v(-299.28, 50) * mm});
            skLineSegment(sketch, "E71.right", {"start": v(-294.28, 60) * mm, "end": v(-294.28, 50) * mm});
            skSolve(sketch);
        }
        {
            var Q0;
            Q0 = qSketchRegion(id + "F39", true);
            extrude(context, id + "F40", {"entities" : qUnion([Q0]), "operationType" : NewBodyOperationType.REMOVE, "oppositeDirection" : true, "depth" : 2.5 * mm});
        }
        {
            var Q0;
            Q0=makeQuery(id+"F12.boolean.opBoolean","COPY",FACE,{"derivedFrom":makeQuery(id+"F12.opExtrude","CAP_FACE",FACE,{"disambiguationData":[OSD([sQuery(id+"F0.wireOp",EDGE,"E37"),sQuery(id+"F11.wireOp",EDGE,"E55.bottom"),sQuery(id+"F11.wireOp",EDGE,"E55.top"),sQuery(id+"F11.wireOp",EDGE,"E55.left")])],"isStart":false})});
            var sketch = newSketch(context, id + "F41", { "sketchPlane" : qUnion([Q0])});
            skLineSegment(sketch, "E72.bottom", {"start": v(-314.28, 60) * mm, "end": v(-309.28, 60) * mm});
            skLineSegment(sketch, "E72.top", {"start": v(-314.28, 50) * mm, "end": v(-309.28, 50) * mm});
            skLineSegment(sketch, "E72.left", {"start": v(-314.28, 60) * mm, "end": v(-314.28, 50) * mm});
            skLineSegment(sketch, "E72.right", {"start": v(-309.28, 60) * mm, "end": v(-309.28, 50) * mm});
            skSolve(sketch);
        }
        {
            var Q0;
            Q0 = qSketchRegion(id + "F41", true);
            extrude(context, id + "F42", {"entities" : qUnion([Q0]), "operationType" : NewBodyOperationType.ADD, "depth" : 2.5 * mm});
        }
        {
            var Q0;
            Q0=makeQuery(id+"F12.boolean.opBoolean","COPY",FACE,{"derivedFrom":makeQuery(id+"F12.opExtrude","CAP_FACE",FACE,{"disambiguationData":[OSD([sQuery(id+"F0.wireOp",EDGE,"E39"),sQuery(id+"F11.wireOp",EDGE,"E55.bottom"),sQuery(id+"F11.wireOp",EDGE,"E55.top"),sQuery(id+"F11.wireOp",EDGE,"E55.right")])],"isStart":false})});
            var sketch = newSketch(context, id + "F43", { "sketchPlane" : qUnion([Q0])});
            skLineSegment(sketch, "E73.bottom", {"start": v(-329.28, 60) * mm, "end": v(-324.28, 60) * mm});
            skLineSegment(sketch, "E73.top", {"start": v(-329.28, 50) * mm, "end": v(-324.28, 50) * mm});
            skLineSegment(sketch, "E73.left", {"start": v(-329.28, 60) * mm, "end": v(-329.28, 50) * mm});
            skLineSegment(sketch, "E73.right", {"start": v(-324.28, 60) * mm, "end": v(-324.28, 50) * mm});
            skSolve(sketch);
        }
        {
            var Q0;
            Q0 = qSketchRegion(id + "F43", true);
            extrude(context, id + "F44", {"entities" : qUnion([Q0]), "operationType" : NewBodyOperationType.REMOVE, "oppositeDirection" : true, "depth" : 2.5 * mm});
        }
        {
            var Q0;
            {var subQ0=sQuery(id+"F0.wireOp",EDGE,"E43");Q0=makeQuery(id+"F10.boolean.opBoolean","MERGE",FACE,{"derivedFrom":[makeQuery(id+"F2.boolean.opBoolean","MERGE",FACE,{"derivedFrom":[makeQuery(id+"F1.opExtrude","SWEPT_FACE",FACE,{"disambiguationData":[OSD([subQ0])]}),makeQuery(id+"F2.opExtrude","SWEPT_FACE",FACE,{"disambiguationData":[OSD([subQ0])]})]}),makeQuery(id+"F10.opExtrude","CAP_FACE",FACE,{"disambiguationData":[OSD([sQuery(id+"F9.wireOp",EDGE,"E54.bottom"),sQuery(id+"F9.wireOp",EDGE,"E54.top"),sQuery(id+"F9.wireOp",EDGE,"E54.left"),sQuery(id+"F9.wireOp",EDGE,"E54.right")])],"isStart":true})]});}
            var sketch = newSketch(context, id + "F45", { "sketchPlane" : qUnion([Q0])});
            skLineSegment(sketch, "E74.bottom", {"start": v(300, -150) * mm, "end": v(82.43, -150) * mm});
            skLineSegment(sketch, "E74.top", {"start": v(300, -18.06) * mm, "end": v(82.43, -18.06) * mm});
            skLineSegment(sketch, "E74.left", {"start": v(300, -150) * mm, "end": v(300, -18.06) * mm});
            skLineSegment(sketch, "E74.right", {"start": v(82.43, -150) * mm, "end": v(82.43, -18.06) * mm});
            skSolve(sketch);
        }
        {
            var Q0;
            Q0 = qSketchRegion(id + "F45", true);
            extrude(context, id + "F46", {"entities" : qUnion([Q0]), "operationType" : NewBodyOperationType.REMOVE, "oppositeDirection" : true, "depth" : 5 * mm});
        }
    });
